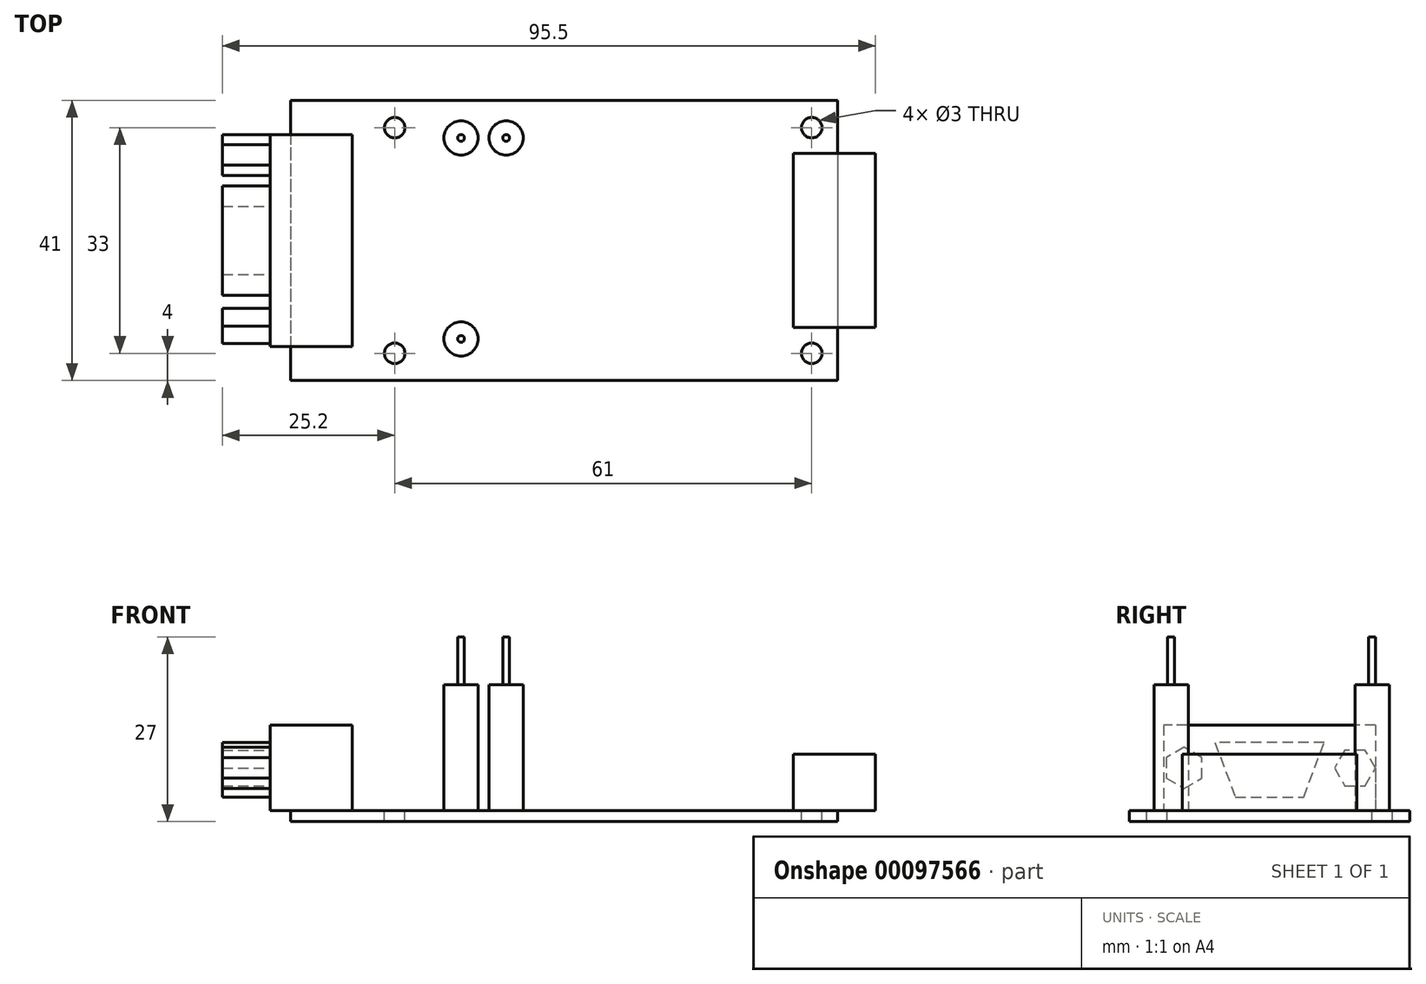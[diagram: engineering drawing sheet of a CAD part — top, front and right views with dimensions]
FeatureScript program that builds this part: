
annotation { "Feature Type Name" : "Feature", "Feature Type Description" : "" }
export const myFeature = defineFeature(function(context is Context, id is Id, definition is map)
    precondition{}
    {
        {
            var Q0;
            Q0=qCreatedBy(makeId("Top.planeOp"),FACE);
            var sketch = newSketch(context, id + "F0", { "sketchPlane" : qUnion([Q0])});
            skLineSegment(sketch, "E0.bottom", {"start": v(-40, 20.5) * mm, "end": v(40, 20.5) * mm});
            skLineSegment(sketch, "E0.top", {"start": v(-40, -20.5) * mm, "end": v(40, -20.5) * mm});
            skLineSegment(sketch, "E0.left", {"start": v(-40, 20.5) * mm, "end": v(-40, -20.5) * mm});
            skLineSegment(sketch, "E0.right", {"start": v(40, 20.5) * mm, "end": v(40, -20.5) * mm});
            skPoint(sketch, "E0.middle", {"position": v(0, 0) * mm});
            skSolve(sketch);
        }
        {
            var Q0;
            Q0 = qSketchRegion(id + "F0", true);
            extrude(context, id + "F1", {"entities" : qUnion([Q0]), "depth" : 1.6 * mm});
        }
        {
            var Q0;
            Q0=makeQuery(id+"F1.opExtrude","CAP_FACE",FACE,{"disambiguationData":[OSD([sQuery(id+"F0.wireOp",EDGE,"E0.bottom"),sQuery(id+"F0.wireOp",EDGE,"E0.top"),sQuery(id+"F0.wireOp",EDGE,"E0.left"),sQuery(id+"F0.wireOp",EDGE,"E0.right")])],"isStart":false});
            var sketch = newSketch(context, id + "F2", { "sketchPlane" : qUnion([Q0])});
            skLineSegment(sketch, "E1", {"start": v(40, 0) * mm, "end": v(40, 12.75) * mm});
            skLineSegment(sketch, "E2", {"start": v(40, 12.75) * mm, "end": v(45.5, 12.75) * mm});
            skLineSegment(sketch, "E3", {"start": v(45.5, 12.75) * mm, "end": v(45.5, -12.75) * mm});
            skLineSegment(sketch, "E4", {"start": v(45.5, -12.75) * mm, "end": v(40, -12.75) * mm});
            skLineSegment(sketch, "E5", {"start": v(40, -12.75) * mm, "end": v(40, 0) * mm});
            skLineSegment(sketch, "E6", {"start": v(40, 12.75) * mm, "end": v(33.5, 12.75) * mm});
            skLineSegment(sketch, "E7", {"start": v(33.5, 12.75) * mm, "end": v(33.5, -12.75) * mm});
            skLineSegment(sketch, "E8", {"start": v(33.5, -12.75) * mm, "end": v(40, -12.75) * mm});
            skSolve(sketch);
        }
        {
            var Q0;
            Q0 = qSketchRegion(id + "F2", true);
            extrude(context, id + "F3", {"entities" : qUnion([Q0]), "operationType" : NewBodyOperationType.ADD, "depth" : 8.24 * mm});
        }
        {
            var Q0;
            Q0=makeQuery(id+"F1.opExtrude","CAP_FACE",FACE,{"disambiguationData":[OSD([sQuery(id+"F0.wireOp",EDGE,"E0.bottom"),sQuery(id+"F0.wireOp",EDGE,"E0.top"),sQuery(id+"F0.wireOp",EDGE,"E0.left"),sQuery(id+"F0.wireOp",EDGE,"E0.right")])],"isStart":false});
            var sketch = newSketch(context, id + "F4", { "sketchPlane" : qUnion([Q0])});
            skLineSegment(sketch, "E9", {"start": v(-40, 0) * mm, "end": v(-40, 15.5) * mm});
            skLineSegment(sketch, "E10", {"start": v(-40, 15.5) * mm, "end": v(-43, 15.5) * mm});
            skLineSegment(sketch, "E11", {"start": v(-43, 15.5) * mm, "end": v(-43, -15.5) * mm});
            skLineSegment(sketch, "E12", {"start": v(-43, -15.5) * mm, "end": v(-40, -15.5) * mm});
            skLineSegment(sketch, "E13", {"start": v(-40, -15.5) * mm, "end": v(-40, 0) * mm});
            skLineSegment(sketch, "E14", {"start": v(-40, 15.5) * mm, "end": v(-31, 15.5) * mm});
            skLineSegment(sketch, "E15", {"start": v(-31, 15.5) * mm, "end": v(-31, -15.5) * mm});
            skLineSegment(sketch, "E16", {"start": v(-31, -15.5) * mm, "end": v(-40, -15.5) * mm});
            skSolve(sketch);
        }
        {
            var Q0;
            Q0 = qSketchRegion(id + "F4", true);
            extrude(context, id + "F5", {"entities" : qUnion([Q0]), "operationType" : NewBodyOperationType.ADD, "depth" : 12.5 * mm});
        }
        {
            var Q0;
            Q0=makeQuery(id+"F5.opExtrude","SWEPT_FACE",FACE,{"disambiguationData":[OSD([sQuery(id+"F4.wireOp",EDGE,"E11")])]});
            var sketch = newSketch(context, id + "F6", { "sketchPlane" : qUnion([Q0])});
            skLineSegment(sketch, "E17", {"start": v(0, 1.6) * mm, "end": v(0, 3.6) * mm});
            skPoint(sketch, "E17.endSnap0", {"position": v(0, 1.6) * mm});
            skLineSegment(sketch, "E18", {"start": v(0, 3.6) * mm, "end": v(-5, 3.6) * mm});
            skLineSegment(sketch, "E19", {"start": v(-5, 3.6) * mm, "end": v(-8, 11.6) * mm});
            skLineSegment(sketch, "E20", {"start": v(-8, 11.6) * mm, "end": v(0, 11.6) * mm});
            skLineSegment(sketch, "E21", {"start": v(0, 11.6) * mm, "end": v(8, 11.6) * mm});
            skLineSegment(sketch, "E22", {"start": v(8, 11.6) * mm, "end": v(5, 3.6) * mm});
            skLineSegment(sketch, "E23", {"start": v(5, 3.6) * mm, "end": v(0, 3.6) * mm});
            skLineSegment(sketch, "E24", {"start": v(0, 11.6) * mm, "end": v(0, 3.6) * mm});
            skLineSegment(sketch, "E25", {"start": v(15.5, 1.6) * mm, "end": v(15.5, 7.85) * mm});
            skLineSegment(sketch, "E26", {"start": v(-15.5, 1.6) * mm, "end": v(-15.5, 7.85) * mm});
            skLineSegment(sketch, "E27", {"start": v(-15.5, 7.85) * mm, "end": v(-12.5, 7.85) * mm});
            skCircle(sketch, "E28.cCircle", {"center": v(-12.5, 7.85) * mm, "radius": 3 * mm, "construction": true});
            skLineSegment(sketch, "E28.0", {"start": v(-15.5, 7.85) * mm, "end": v(-14, 10.45) * mm});
            skLineSegment(sketch, "E28.1", {"start": v(-14, 10.45) * mm, "end": v(-11, 10.45) * mm});
            skLineSegment(sketch, "E28.2", {"start": v(-11, 10.45) * mm, "end": v(-9.5, 7.85) * mm});
            skLineSegment(sketch, "E28.3", {"start": v(-9.5, 7.85) * mm, "end": v(-11, 5.25) * mm});
            skLineSegment(sketch, "E28.4", {"start": v(-11, 5.25) * mm, "end": v(-14, 5.25) * mm});
            skLineSegment(sketch, "E28.5", {"start": v(-14, 5.25) * mm, "end": v(-15.5, 7.85) * mm});
            skLineSegment(sketch, "E29", {"start": v(15.5, 7.85) * mm, "end": v(12.5, 7.85) * mm});
            skCircle(sketch, "E30.cCircle", {"center": v(12.5, 7.85) * mm, "radius": 3 * mm, "construction": true});
            skLineSegment(sketch, "E30.0", {"start": v(12.5, 10.85) * mm, "end": v(15.1, 9.35) * mm});
            skLineSegment(sketch, "E30.1", {"start": v(15.1, 9.35) * mm, "end": v(15.1, 6.35) * mm});
            skLineSegment(sketch, "E30.2", {"start": v(15.1, 6.35) * mm, "end": v(12.5, 4.85) * mm});
            skLineSegment(sketch, "E30.3", {"start": v(12.5, 4.85) * mm, "end": v(9.9, 6.35) * mm});
            skLineSegment(sketch, "E30.4", {"start": v(9.9, 6.35) * mm, "end": v(9.9, 9.35) * mm});
            skLineSegment(sketch, "E30.5", {"start": v(9.9, 9.35) * mm, "end": v(12.5, 10.85) * mm});
            skSolve(sketch);
        }
        {
            var Q0;
            Q0 = qSketchRegion(id + "F6", true);
            extrude(context, id + "F7", {"entities" : qUnion([Q0]), "operationType" : NewBodyOperationType.ADD, "depth" : 7 * mm});
        }
        {
            var Q0;
            Q0=makeQuery(id+"F1.opExtrude","CAP_FACE",FACE,{"disambiguationData":[OSD([sQuery(id+"F0.wireOp",EDGE,"E0.bottom"),sQuery(id+"F0.wireOp",EDGE,"E0.top"),sQuery(id+"F0.wireOp",EDGE,"E0.left"),sQuery(id+"F0.wireOp",EDGE,"E0.right")])],"isStart":false});
            var sketch = newSketch(context, id + "F8", { "sketchPlane" : qUnion([Q0])});
            skLineSegment(sketch, "E31", {"start": v(40, 20.5) * mm, "end": v(36.2, 20.5) * mm});
            skLineSegment(sketch, "E32", {"start": v(36.2, 20.5) * mm, "end": v(36.2, 16.5) * mm});
            skLineSegment(sketch, "E33", {"start": v(-40, 20.5) * mm, "end": v(-24.8, 20.5) * mm});
            skLineSegment(sketch, "E34", {"start": v(-40, -20.5) * mm, "end": v(-24.8, -20.5) * mm});
            skLineSegment(sketch, "E35", {"start": v(40, -20.5) * mm, "end": v(36.2, -20.5) * mm});
            skLineSegment(sketch, "E36", {"start": v(36.2, -20.5) * mm, "end": v(36.2, -16.5) * mm});
            skCircle(sketch, "E37", {"center": v(36.2, 16.5) * mm, "radius": 1.5 * mm});
            skCircle(sketch, "E38", {"center": v(36.2, -16.5) * mm, "radius": 1.5 * mm});
            skLineSegment(sketch, "E39", {"start": v(36.2, 16.5) * mm, "end": v(36.2, 0) * mm});
            skLineSegment(sketch, "E40", {"start": v(36.2, 0) * mm, "end": v(36.2, -16.5) * mm});
            skLineSegment(sketch, "E41", {"start": v(-24.8, 20.5) * mm, "end": v(-24.8, 16.5) * mm});
            skLineSegment(sketch, "E42", {"start": v(-24.8, -20.5) * mm, "end": v(-24.8, -16.5) * mm});
            skCircle(sketch, "E43", {"center": v(-24.8, 16.5) * mm, "radius": 1.5 * mm});
            skCircle(sketch, "E44", {"center": v(-24.8, -16.5) * mm, "radius": 1.5 * mm});
            skLineSegment(sketch, "E45", {"start": v(-24.8, -20.5) * mm, "end": v(36.2, -20.5) * mm});
            skSolve(sketch);
        }
        {
            var Q0;
            Q0 = qSketchRegion(id + "F8", true);
            extrude(context, id + "F9", {"entities" : qUnion([Q0]), "operationType" : NewBodyOperationType.REMOVE, "oppositeDirection" : true, "depth" : 2 * mm});
        }
        {
            var Q0;
            Q0=makeQuery(id+"F1.opExtrude","CAP_FACE",FACE,{"disambiguationData":[OSD([sQuery(id+"F0.wireOp",EDGE,"E0.bottom"),sQuery(id+"F0.wireOp",EDGE,"E0.top"),sQuery(id+"F0.wireOp",EDGE,"E0.left"),sQuery(id+"F0.wireOp",EDGE,"E0.right")])],"isStart":false});
            var sketch = newSketch(context, id + "F10", { "sketchPlane" : qUnion([Q0])});
            skLineSegment(sketch, "E46", {"start": v(-40, 20.5) * mm, "end": v(-8.5, 20.5) * mm});
            skLineSegment(sketch, "E47", {"start": v(-8.5, 20.5) * mm, "end": v(-8.5, 15) * mm});
            skLineSegment(sketch, "E48", {"start": v(-8.5, 15) * mm, "end": v(-15.1, 15) * mm});
            skLineSegment(sketch, "E49", {"start": v(-40, -20.5) * mm, "end": v(-15.1, -20.5) * mm});
            skLineSegment(sketch, "E50", {"start": v(-15.1, -20.5) * mm, "end": v(-15.1, -14.4) * mm});
            skCircle(sketch, "E51", {"center": v(-15.1, 15) * mm, "radius": 2.5 * mm});
            skCircle(sketch, "E52", {"center": v(-8.5, 15) * mm, "radius": 2.5 * mm});
            skCircle(sketch, "E53", {"center": v(-15.1, -14.4) * mm, "radius": 2.5 * mm});
            skLineSegment(sketch, "E54", {"start": v(-15.1, 15) * mm, "end": v(-15.1, 0) * mm});
            skLineSegment(sketch, "E55", {"start": v(-15.1, 0) * mm, "end": v(-15.1, -14.4) * mm});
            skSolve(sketch);
        }
        {
            var Q0;
            Q0 = qSketchRegion(id + "F10", true);
            extrude(context, id + "F11", {"entities" : qUnion([Q0]), "operationType" : NewBodyOperationType.ADD, "depth" : 18.4 * mm});
        }
        {
            var Q0;
            Q0=makeQuery(id+"F11.opExtrude","CAP_FACE",FACE,{"disambiguationData":[OSD([sQuery(id+"F10.wireOp",EDGE,"E51")])],"isStart":false});
            var sketch = newSketch(context, id + "F12", { "sketchPlane" : qUnion([Q0])});
            skCircle(sketch, "E56", {"center": v(-15.1, 15) * mm, "radius": 0.5 * mm});
            skSolve(sketch);
        }
        {
            var Q0;
            Q0 = qSketchRegion(id + "F12", true);
            extrude(context, id + "F13", {"entities" : qUnion([Q0]), "operationType" : NewBodyOperationType.ADD, "depth" : 7 * mm});
        }
        {
            var Q0;
            Q0=makeQuery(id+"F11.opExtrude","CAP_FACE",FACE,{"disambiguationData":[OSD([sQuery(id+"F10.wireOp",EDGE,"E52")])],"isStart":false});
            var sketch = newSketch(context, id + "F14", { "sketchPlane" : qUnion([Q0])});
            skCircle(sketch, "E57", {"center": v(-8.5, 15) * mm, "radius": 0.5 * mm});
            skSolve(sketch);
        }
        {
            var Q0;
            Q0 = qSketchRegion(id + "F14", true);
            extrude(context, id + "F15", {"entities" : qUnion([Q0]), "operationType" : NewBodyOperationType.ADD, "depth" : 7 * mm});
        }
        {
            var Q0;
            Q0=makeQuery(id+"F11.opExtrude","CAP_FACE",FACE,{"disambiguationData":[OSD([sQuery(id+"F10.wireOp",EDGE,"E53")])],"isStart":false});
            var sketch = newSketch(context, id + "F16", { "sketchPlane" : qUnion([Q0])});
            skCircle(sketch, "E58", {"center": v(-15.1, -14.4) * mm, "radius": 0.5 * mm});
            skSolve(sketch);
        }
        {
            var Q0;
            Q0 = qSketchRegion(id + "F16", true);
            extrude(context, id + "F17", {"entities" : qUnion([Q0]), "operationType" : NewBodyOperationType.ADD, "depth" : 7 * mm});
        }
    });
